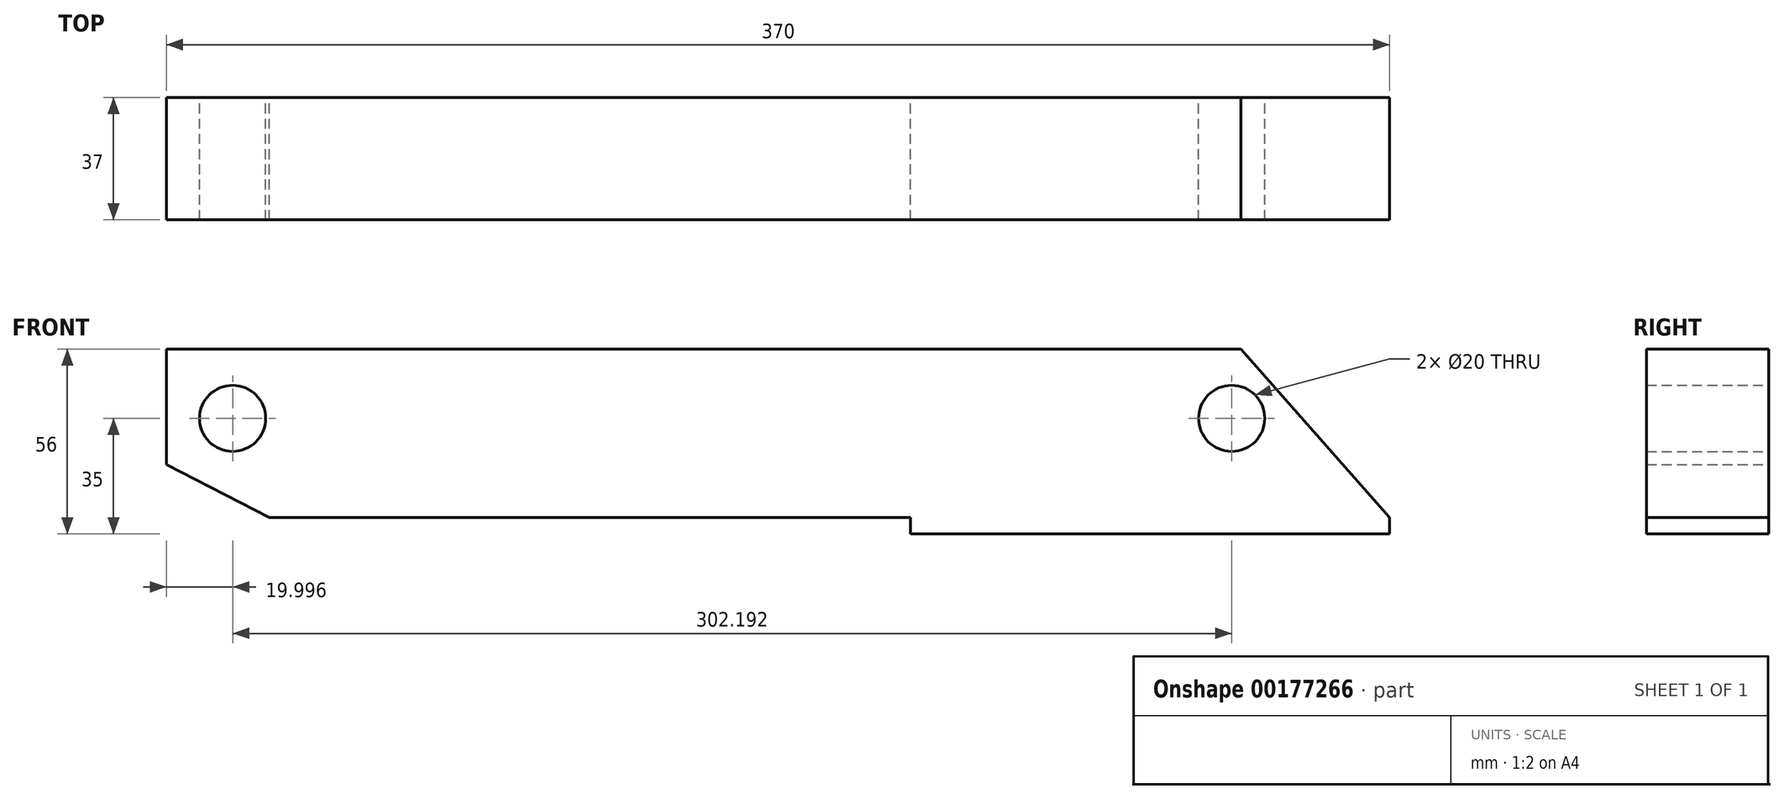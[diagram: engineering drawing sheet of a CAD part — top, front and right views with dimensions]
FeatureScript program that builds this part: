
annotation { "Feature Type Name" : "Feature", "Feature Type Description" : "" }
export const myFeature = defineFeature(function(context is Context, id is Id, definition is map)
    precondition{}
    {
        {
            var Q0;
            Q0=qCreatedBy(makeId("Front.planeOp"),FACE);
            var sketch = newSketch(context, id + "F0", { "sketchPlane" : qUnion([Q0])});
            skLineSegment(sketch, "E0", {"start": v(-160.43, 0) * mm, "end": v(178.44, 0) * mm});
            skLineSegment(sketch, "E1", {"start": v(178.44, 0) * mm, "end": v(133.44, 51) * mm});
            skLineSegment(sketch, "E2", {"start": v(133.44, 51) * mm, "end": v(-191.56, 51) * mm});
            skLineSegment(sketch, "E3", {"start": v(-191.56, 51) * mm, "end": v(-191.56, 16) * mm});
            skLineSegment(sketch, "E4", {"start": v(-191.56, 16) * mm, "end": v(-160.43, 0) * mm});
            skCircle(sketch, "E5", {"center": v(-171.56, 30) * mm, "radius": 10 * mm});
            skCircle(sketch, "E6", {"center": v(130.63, 30) * mm, "radius": 10 * mm});
            skLineSegment(sketch, "E7", {"start": v(-248.51, 30) * mm, "end": v(170.76, 30) * mm, "construction": true});
            skSolve(sketch);
        }
        {
            var Q0;
            Q0=makeQuery(id+"F0.imprint","IMPRINT",FACE,{"disambiguationData":[TD([[makeQuery(id+"F0.imprint","IMPRINT",EDGE,{"derivedFrom":sQuery(id+"F0.wireOp",EDGE,"E0")}),1.0]])]});
            extrude(context, id + "F1", {"entities" : qUnion([Q0]), "depth" : 37 * mm});
        }
        {
            var Q0;
            Q0=qCreatedBy(makeId("Top.planeOp"),FACE);
            var sketch = newSketch(context, id + "F2", { "sketchPlane" : qUnion([Q0])});
            skLineSegment(sketch, "E8.bottom", {"start": v(178.44, -37) * mm, "end": v(33.44, -37) * mm});
            skLineSegment(sketch, "E8.top", {"start": v(178.44, 0) * mm, "end": v(33.44, 0) * mm});
            skLineSegment(sketch, "E8.left", {"start": v(178.44, -37) * mm, "end": v(178.44, 0) * mm});
            skLineSegment(sketch, "E8.right", {"start": v(33.44, -37) * mm, "end": v(33.44, 0) * mm});
            skPoint(sketch, "E9", {"position": v(178.44, 0) * mm});
            skSolve(sketch);
        }
        {
            var Q0;
            Q0 = qSketchRegion(id + "F2", true);
            extrude(context, id + "F3", {"entities" : qUnion([Q0]), "operationType" : NewBodyOperationType.ADD, "oppositeDirection" : true, "depth" : 5 * mm});
        }
    });
